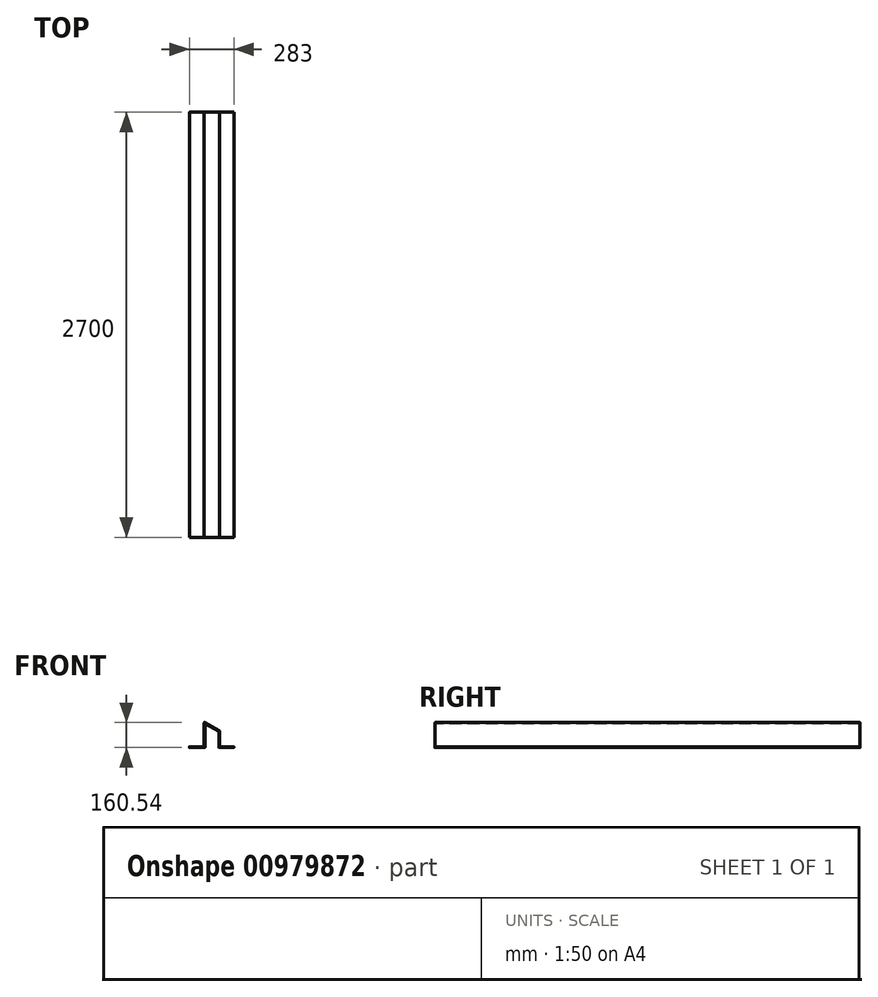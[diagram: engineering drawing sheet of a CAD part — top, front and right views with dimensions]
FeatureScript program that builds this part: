
annotation { "Feature Type Name" : "Feature", "Feature Type Description" : "" }
export const myFeature = defineFeature(function(context is Context, id is Id, definition is map)
    precondition{}
    {
        {
            var Q0;
            Q0=qCreatedBy(makeId("Front.planeOp"),FACE);
            var sketch = newSketch(context, id + "F0", { "sketchPlane" : qUnion([Q0])});
            skLineSegment(sketch, "E0", {"start": v(0, 0) * mm, "end": v(-95, 0) * mm});
            skLineSegment(sketch, "E1", {"start": v(-95, 0) * mm, "end": v(-95, 102.53) * mm});
            skLineSegment(sketch, "E2", {"start": v(-95, 102.53) * mm, "end": v(-183, 153.34) * mm});
            skLineSegment(sketch, "E3", {"start": v(-183, 153.34) * mm, "end": v(-183, 0) * mm});
            skLineSegment(sketch, "E4", {"start": v(-183, 0) * mm, "end": v(-283, 0) * mm});
            skLineSegment(sketch, "E5", {"start": v(-283, 0) * mm, "end": v(-283, 5) * mm});
            skLineSegment(sketch, "E6", {"start": v(-283, 5) * mm, "end": v(-188, 5) * mm});
            skLineSegment(sketch, "E7", {"start": v(-188, 5) * mm, "end": v(-188, 162) * mm});
            skLineSegment(sketch, "E8", {"start": v(-188, 162) * mm, "end": v(-90, 105.42) * mm});
            skLineSegment(sketch, "E9", {"start": v(-90, 105.42) * mm, "end": v(-90, 5) * mm});
            skLineSegment(sketch, "E10", {"start": v(-90, 5) * mm, "end": v(0, 5) * mm});
            skLineSegment(sketch, "E11", {"start": v(0, 5) * mm, "end": v(0, 0) * mm});
            skLineSegment(sketch, "E12", {"start": v(-188, 5) * mm, "end": v(-183, 5) * mm, "construction": true});
            skLineSegment(sketch, "E13", {"start": v(-95, 5) * mm, "end": v(-90, 5) * mm, "construction": true});
            skLineSegment(sketch, "E14", {"start": v(-183, 153.34) * mm, "end": v(-180.5, 157.67) * mm, "construction": true});
            skLineSegment(sketch, "E15", {"start": v(-183, 0) * mm, "end": v(-95, 0) * mm, "construction": true});
            skSolve(sketch);
        }
        {
            var Q0;
            Q0 = qSketchRegion(id + "F0", true);
            extrude(context, id + "F1", {"entities" : qUnion([Q0]), "depth" : 2700 * mm, "offsetDistance" : 25 * mm});
        }
        {
            var Q0;
            Q0=makeQuery(id+"F1.opExtrude","CAP_FACE",FACE,{"disambiguationData":[OSD([sQuery(id+"F0.wireOp",EDGE,"E0"),sQuery(id+"F0.wireOp",EDGE,"E1"),sQuery(id+"F0.wireOp",EDGE,"E2"),sQuery(id+"F0.wireOp",EDGE,"E3"),sQuery(id+"F0.wireOp",EDGE,"E4"),sQuery(id+"F0.wireOp",EDGE,"E5"),sQuery(id+"F0.wireOp",EDGE,"E6"),sQuery(id+"F0.wireOp",EDGE,"E7"),sQuery(id+"F0.wireOp",EDGE,"E8"),sQuery(id+"F0.wireOp",EDGE,"E9"),sQuery(id+"F0.wireOp",EDGE,"E10"),sQuery(id+"F0.wireOp",EDGE,"E11")])],"isStart":false});
            cPlane(context, id + "F2", {"entities" : qUnion([Q0]), "cplaneType" : CPlaneType.OFFSET, "offset" : 150 * mm, "oppositeDirection" : true, "width" : 150 * mm, "height" : 150 * mm});
        }
        {
            var Q0;
            Q0=makeQuery(id+"F1.opExtrude","SWEPT_FACE",FACE,{"disambiguationData":[OSD([sQuery(id+"F0.wireOp",EDGE,"E10")])]});
            var Q1;
            Q1=makeQuery(id+"F1.opExtrude","SWEPT_FACE",FACE,{"disambiguationData":[OSD([sQuery(id+"F0.wireOp",EDGE,"E9")])]});
            var Q2;
            Q2=makeQuery(id+"F1.opExtrude","SWEPT_FACE",FACE,{"disambiguationData":[OSD([sQuery(id+"F0.wireOp",EDGE,"E8")])]});
            var Q3;
            Q3=makeQuery(id+"F1.opExtrude","SWEPT_FACE",FACE,{"disambiguationData":[OSD([sQuery(id+"F0.wireOp",EDGE,"E7")])]});
            var Q4;
            Q4=makeQuery(id+"F1.opExtrude","SWEPT_EDGE",EDGE,{"disambiguationData":[OSD([sQuery(id+"F0.wireOp",EDGE,"E5"),sQuery(id+"F0.wireOp",EDGE,"E6")])]});
            var Q5;
            Q5=makeQuery(id+"F1.opExtrude","SWEPT_FACE",FACE,{"disambiguationData":[OSD([sQuery(id+"F0.wireOp",EDGE,"E6")])]});
            var Q6;
            Q6=makeQuery(id+"F1.opExtrude","SWEPT_FACE",FACE,{"disambiguationData":[OSD([sQuery(id+"F0.wireOp",EDGE,"E0")])]});
            var Q7;
            Q7=makeQuery(id+"F1.opExtrude","SWEPT_FACE",FACE,{"disambiguationData":[OSD([sQuery(id+"F0.wireOp",EDGE,"E3")])]});
            var Q8;
            Q8=makeQuery(id+"F1.opExtrude","SWEPT_FACE",FACE,{"disambiguationData":[OSD([sQuery(id+"F0.wireOp",EDGE,"E2")])]});
            var Q9;
            Q9=makeQuery(id+"F1.opExtrude","SWEPT_FACE",FACE,{"disambiguationData":[OSD([sQuery(id+"F0.wireOp",EDGE,"E4")])]});
            var Q10;
            Q10=makeQuery(id+"F1.opExtrude","SWEPT_FACE",FACE,{"disambiguationData":[OSD([sQuery(id+"F0.wireOp",EDGE,"E1")])]});
            fillet(context, id + "F3", {"entities" : qUnion([Q0, Q1, Q2, Q3, Q4, Q5, Q6, Q7, Q8, Q9, Q10]), "radius" : 2 * mm, "tangentPropagation" : true, "allowEdgeOverflow" : false});
        }
    });
